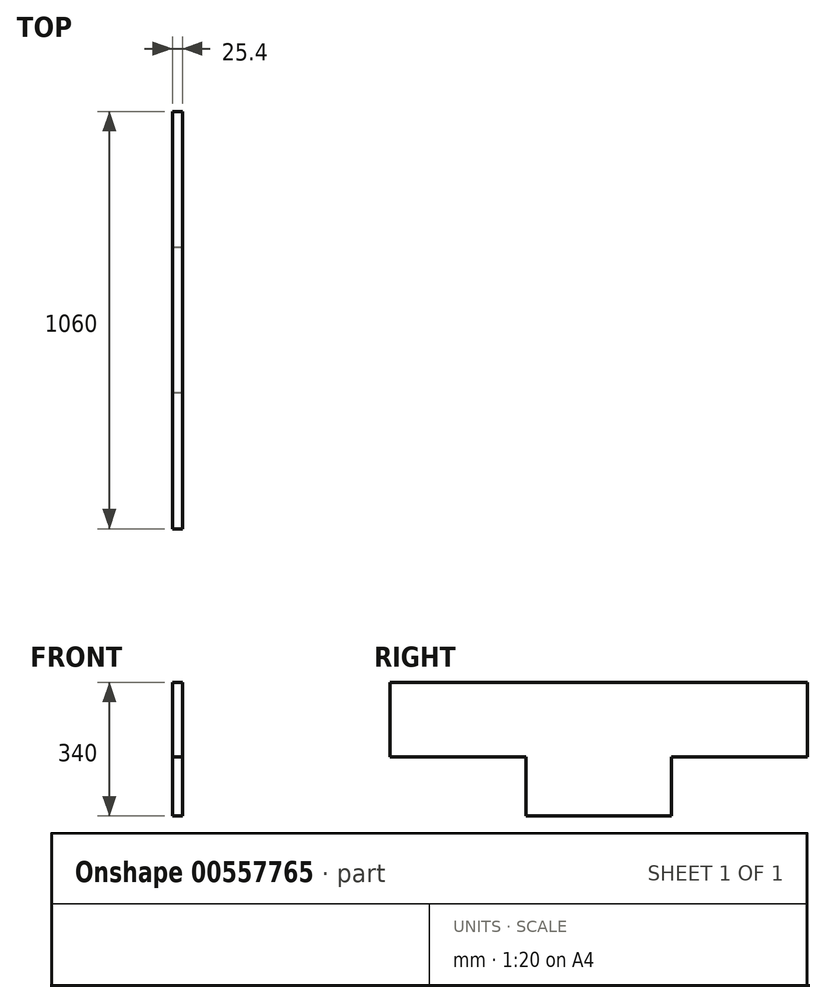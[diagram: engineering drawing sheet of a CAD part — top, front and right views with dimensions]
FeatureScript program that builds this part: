
annotation { "Feature Type Name" : "Feature", "Feature Type Description" : "" }
export const myFeature = defineFeature(function(context is Context, id is Id, definition is map)
    precondition{}
    {
        {
            var Q0;
            Q0=qCreatedBy(makeId("Right.planeOp"),FACE);
            var sketch = newSketch(context, id + "F0", { "sketchPlane" : qUnion([Q0])});
            skLineSegment(sketch, "E0.bottom", {"start": v(-230.36, 182.6) * mm, "end": v(139.64, 182.6) * mm});
            skLineSegment(sketch, "E0.top", {"start": v(-230.36, -37.4) * mm, "end": v(139.64, -37.4) * mm});
            skLineSegment(sketch, "E0.left", {"start": v(-230.36, 182.6) * mm, "end": v(-230.36, -37.4) * mm});
            skLineSegment(sketch, "E0.right", {"start": v(139.64, 182.6) * mm, "end": v(139.64, -37.4) * mm});
            skLineSegment(sketch, "E1.bottom", {"start": v(-575.36, 182.6) * mm, "end": v(-230.36, 182.6) * mm});
            skLineSegment(sketch, "E1.top", {"start": v(-575.36, -7.4) * mm, "end": v(-230.36, -7.4) * mm});
            skLineSegment(sketch, "E1.left", {"start": v(-575.36, 182.6) * mm, "end": v(-575.36, -7.4) * mm});
            skLineSegment(sketch, "E1.right", {"start": v(-230.36, 182.6) * mm, "end": v(-230.36, -7.4) * mm});
            skLineSegment(sketch, "E2.bottom", {"start": v(139.64, -37.4) * mm, "end": v(-230.36, -37.4) * mm});
            skLineSegment(sketch, "E2.top", {"start": v(139.64, -157.4) * mm, "end": v(-230.36, -157.4) * mm});
            skLineSegment(sketch, "E2.left", {"start": v(139.64, -157.4) * mm, "end": v(139.64, -37.4) * mm});
            skLineSegment(sketch, "E2.right", {"start": v(-230.36, -157.4) * mm, "end": v(-230.36, -37.4) * mm});
            skLineSegment(sketch, "E3.bottom", {"start": v(139.64, 182.6) * mm, "end": v(484.64, 182.6) * mm});
            skLineSegment(sketch, "E3.top", {"start": v(139.64, -7.4) * mm, "end": v(484.64, -7.4) * mm});
            skLineSegment(sketch, "E3.left", {"start": v(139.64, 182.6) * mm, "end": v(139.64, -7.4) * mm});
            skLineSegment(sketch, "E3.right", {"start": v(484.64, 182.6) * mm, "end": v(484.64, -7.4) * mm});
            skSolve(sketch);
        }
        {
            var Q0;
            Q0 = qSketchRegion(id + "F0", true);
            extrude(context, id + "F1", {"entities" : qUnion([Q0]), "depth" : 25.4 * mm, "offsetDistance" : 25.4 * mm});
        }
    });
